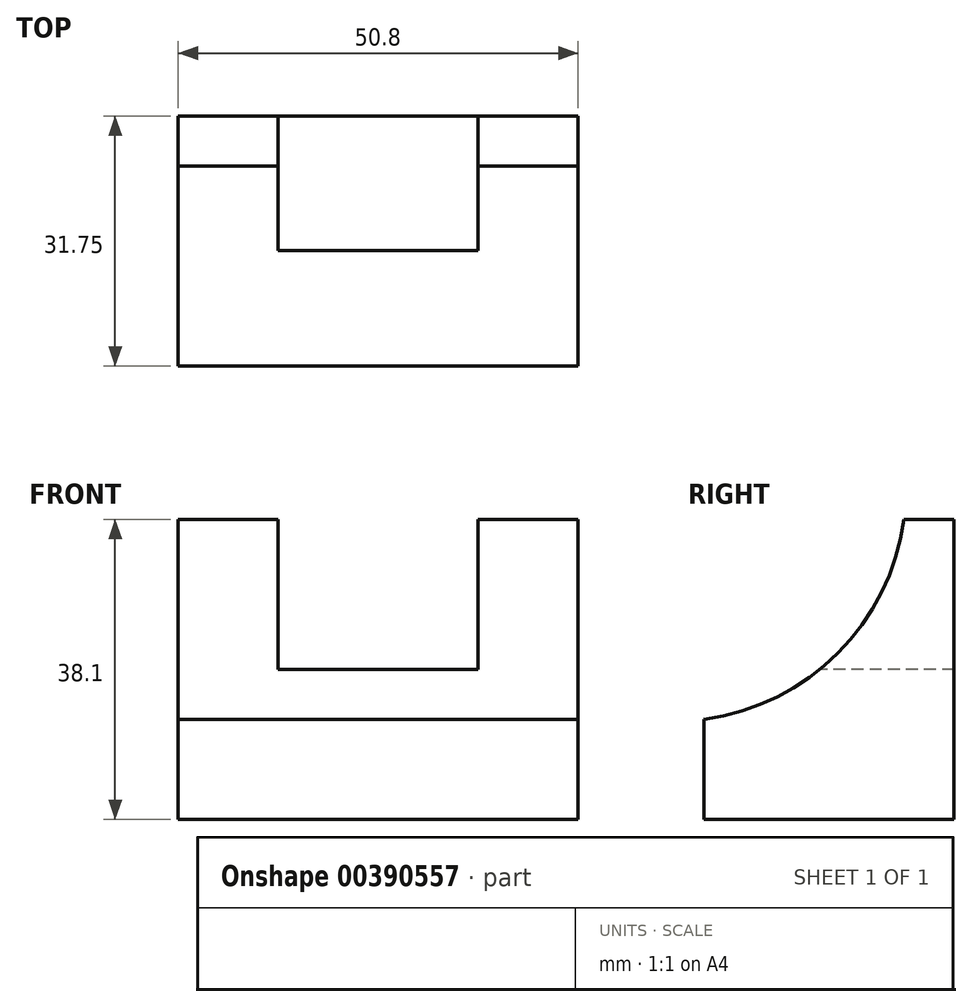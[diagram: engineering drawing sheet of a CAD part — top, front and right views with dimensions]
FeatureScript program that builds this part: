
annotation { "Feature Type Name" : "Feature", "Feature Type Description" : "" }
export const myFeature = defineFeature(function(context is Context, id is Id, definition is map)
    precondition{}
    {
        {
            var Q0;
            Q0=qCreatedBy(makeId("Front.planeOp"),FACE);
            var sketch = newSketch(context, id + "F0", { "sketchPlane" : qUnion([Q0])});
            skLineSegment(sketch, "E0", {"start": v(0, 0) * mm, "end": v(50.8, 0) * mm});
            skLineSegment(sketch, "E1", {"start": v(50.8, 0) * mm, "end": v(50.8, 38.1) * mm});
            skLineSegment(sketch, "E2", {"start": v(50.8, 38.1) * mm, "end": v(0, 38.1) * mm});
            skLineSegment(sketch, "E3", {"start": v(0, 38.1) * mm, "end": v(0, 0) * mm});
            skSolve(sketch);
        }
        {
            var Q0;
            Q0 = qSketchRegion(id + "F0", true);
            extrude(context, id + "F1", {"entities" : qUnion([Q0]), "depth" : 31.75 * mm});
        }
        {
            var Q0;
            Q0=makeQuery(id+"F1.opExtrude","CAP_FACE",FACE,{"disambiguationData":[OSD([sQuery(id+"F0.wireOp",EDGE,"E0"),sQuery(id+"F0.wireOp",EDGE,"E1"),sQuery(id+"F0.wireOp",EDGE,"E2"),sQuery(id+"F0.wireOp",EDGE,"E3")])],"isStart":false});
            var sketch = newSketch(context, id + "F2", { "sketchPlane" : qUnion([Q0])});
            skLineSegment(sketch, "E4", {"start": v(12.7, 38.1) * mm, "end": v(12.7, 19.05) * mm});
            skLineSegment(sketch, "E5", {"start": v(12.7, 19.05) * mm, "end": v(38.1, 19.05) * mm});
            skLineSegment(sketch, "E6", {"start": v(38.1, 19.05) * mm, "end": v(38.1, 38.1) * mm});
            skSolve(sketch);
        }
        {
            var Q0;
            Q0 = qSketchRegion(id + "F2", true);
            var Q1;
            {var subQ0=sQuery(id+"F2.wireOp",EDGE,"E4");Q1=makeQuery(id+"F2.imprint","IMPRINT",FACE,{"disambiguationData":[TD([[makeQuery(id+"F2.imprint","IMPRINT",EDGE,{"derivedFrom":subQ0}),1.0]])]});}
            extrude(context, id + "F3", {"entities" : qUnion([Q0, Q1]), "operationType" : NewBodyOperationType.REMOVE, "oppositeDirection" : true, "depth" : 31.75 * mm});
        }
        {
            var Q0;
            Q0=makeQuery(id+"F1.opExtrude","SWEPT_FACE",FACE,{"disambiguationData":[OSD([sQuery(id+"F0.wireOp",EDGE,"E1")])]});
            var sketch = newSketch(context, id + "F4", { "sketchPlane" : qUnion([Q0])});
            skArc(sketch, "E7", {"start": v(-31.75, 12.7) * mm, "mid": v(-14.77, 21.12) * mm, "end": v(-6.35, 38.1) * mm});
            skSolve(sketch);
        }
        {
            var Q0;
            Q0 = qSketchRegion(id + "F4", true);
            var Q1;
            {var subQ0=sQuery(id+"F4.wireOp",EDGE,"E7");Q1=makeQuery(id+"F4.imprint","IMPRINT",FACE,{"disambiguationData":[TD([[makeQuery(id+"F4.imprint","IMPRINT",EDGE,{"derivedFrom":subQ0}),1.0]])]});}
            extrude(context, id + "F5", {"entities" : qUnion([Q0, Q1]), "operationType" : NewBodyOperationType.REMOVE, "oppositeDirection" : true, "depth" : 50.8 * mm});
        }
    });
